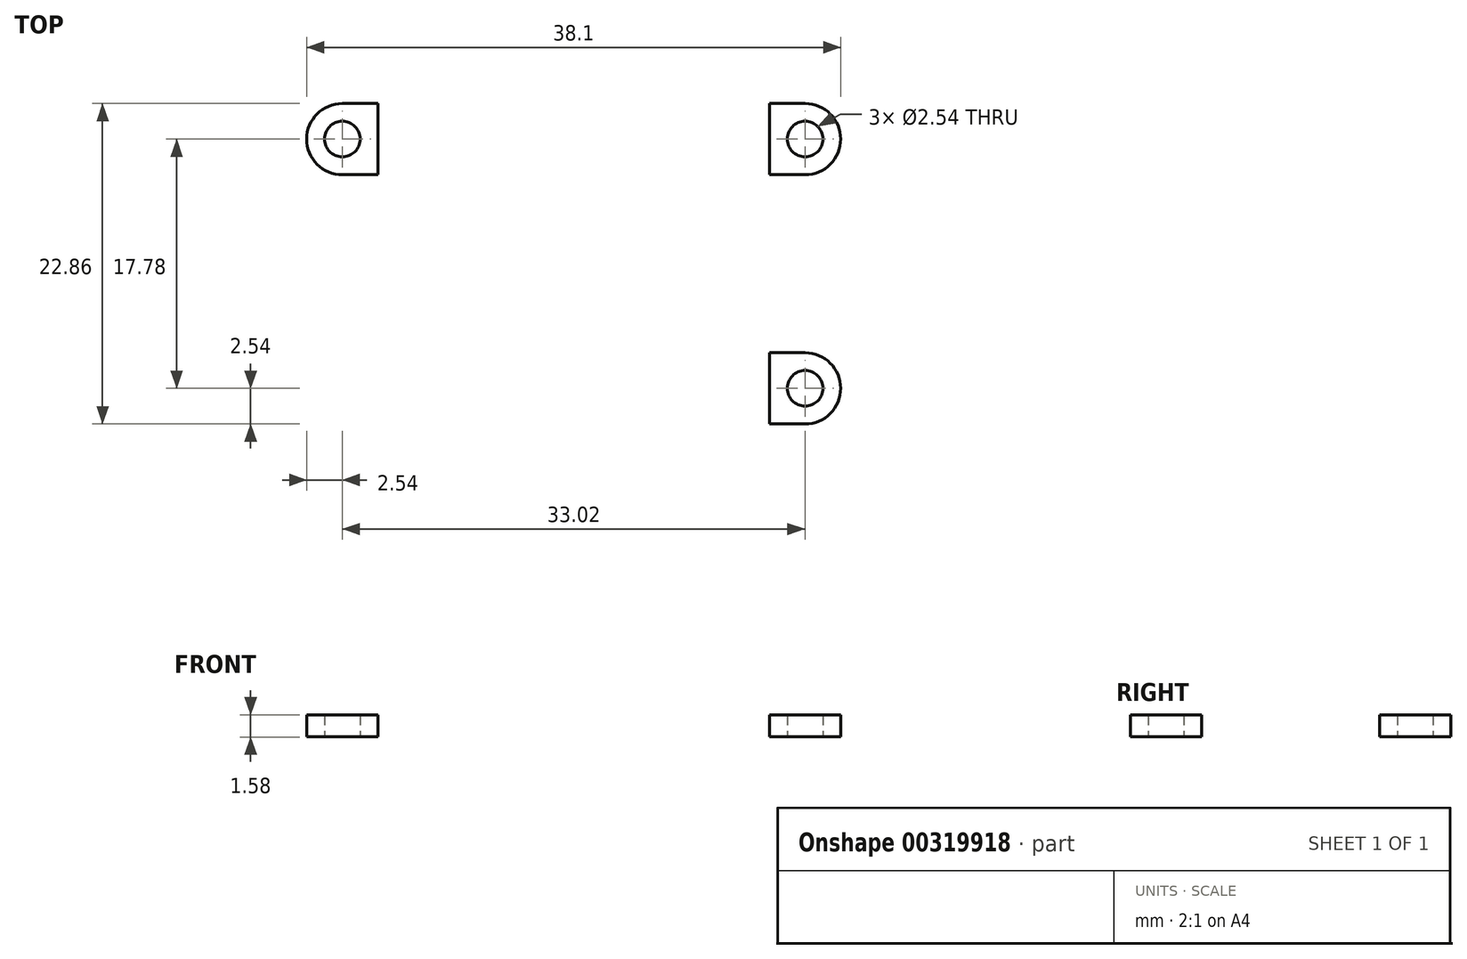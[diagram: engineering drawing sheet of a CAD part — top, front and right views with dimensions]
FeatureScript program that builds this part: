
annotation { "Feature Type Name" : "Feature", "Feature Type Description" : "" }
export const myFeature = defineFeature(function(context is Context, id is Id, definition is map)
    precondition{}
    {
        {
            var Q0;
            Q0=qCreatedBy(makeId("Top.planeOp"),FACE);
            var sketch = newSketch(context, id + "F0", { "sketchPlane" : qUnion([Q0])});
            skLineSegment(sketch, "E0.bottom", {"start": v(16.51, 11.43) * mm, "end": v(-16.51, 11.43) * mm});
            skLineSegment(sketch, "E0.top", {"start": v(16.51, -11.43) * mm, "end": v(-13.97, -11.43) * mm});
            skLineSegment(sketch, "E0.right", {"start": v(-19.05, 8.89) * mm, "end": v(-19.05, 8.89) * mm});
            skPoint(sketch, "E0.middle", {"position": v(0, 0) * mm});
            skLineSegment(sketch, "E1", {"start": v(-13.97, 11.43) * mm, "end": v(-13.97, -11.43) * mm});
            skLineSegment(sketch, "E2", {"start": v(-16.5, 6.35) * mm, "end": v(-13.97, 6.35) * mm});
            skCircle(sketch, "E3", {"center": v(-16.5, 8.89) * mm, "radius": 1.27 * mm});
            skPoint(sketch, "E3.centerSnap0", {"position": v(-16.5, 6.35) * mm});
            skPoint(sketch, "E3.centerSnap1", {"position": v(-19.05, 8.89) * mm});
            skPoint(sketch, "E4.visualSharp", {"position": v(-19.05, 11.43) * mm});
            skArc(sketch, "E4.filletArc", {"start": v(-16.51, 11.43) * mm, "mid": v(-18.3, 10.69) * mm, "end": v(-19.05, 8.89) * mm});
            skPoint(sketch, "E5.visualSharp", {"position": v(-19.05, 6.35) * mm});
            skArc(sketch, "E5.filletArc", {"start": v(-19.05, 8.89) * mm, "mid": v(-18.3, 7.1) * mm, "end": v(-16.5, 6.35) * mm});
            skLineSegment(sketch, "E6", {"start": v(-16.51, 11.43) * mm, "end": v(-13.97, 11.43) * mm});
            skPoint(sketch, "E7.MirrorP", {"position": v(-19.05, -8.89) * mm});
            skPoint(sketch, "E8.MirrorP", {"position": v(-19.05, -6.35) * mm});
            skCircle(sketch, "E9.MirrorC", {"center": v(-16.5, -8.89) * mm, "radius": 1.27 * mm});
            skArc(sketch, "E10.MirrorCS", {"start": v(-16.51, -11.43) * mm, "mid": v(-18.3, -10.69) * mm, "end": v(-19.05, -8.89) * mm});
            skPoint(sketch, "E11.MirrorP", {"position": v(-19.05, -11.43) * mm});
            skArc(sketch, "E12.MirrorCS", {"start": v(-19.05, -8.89) * mm, "mid": v(-18.3, -7.1) * mm, "end": v(-16.5, -6.35) * mm});
            skPoint(sketch, "E13.MirrorP", {"position": v(-16.5, -6.35) * mm});
            skLineSegment(sketch, "E14.MirrorCS", {"start": v(-16.5, -6.35) * mm, "end": v(-13.97, -6.35) * mm});
            skLineSegment(sketch, "E15.MirrorCS", {"start": v(-16.51, -11.43) * mm, "end": v(-13.97, -11.43) * mm});
            skLineSegment(sketch, "E16.MirrorCS", {"start": v(-13.97, -11.43) * mm, "end": v(-13.97, 11.43) * mm});
            skLineSegment(sketch, "E17.MirrorCS", {"start": v(-19.05, -8.89) * mm, "end": v(-19.05, -8.89) * mm});
            skPoint(sketch, "E18.MirrorP", {"position": v(19.05, 8.89) * mm});
            skPoint(sketch, "E19.MirrorP", {"position": v(19.05, -8.89) * mm});
            skPoint(sketch, "E20.MirrorP", {"position": v(16.5, -6.35) * mm});
            skPoint(sketch, "E21.MirrorP", {"position": v(16.5, 6.35) * mm});
            skCircle(sketch, "E22.MirrorC", {"center": v(16.5, 8.89) * mm, "radius": 1.27 * mm});
            skLineSegment(sketch, "E23.MirrorCS", {"start": v(16.5, -6.35) * mm, "end": v(13.97, -6.35) * mm});
            skLineSegment(sketch, "E24.MirrorCS", {"start": v(16.51, -11.43) * mm, "end": v(13.97, -11.43) * mm});
            skArc(sketch, "E25.MirrorCS", {"start": v(19.05, 8.89) * mm, "mid": v(18.3, 7.1) * mm, "end": v(16.5, 6.35) * mm});
            skLineSegment(sketch, "E26.MirrorCS", {"start": v(13.97, -11.43) * mm, "end": v(13.97, 11.43) * mm});
            skArc(sketch, "E27.MirrorCS", {"start": v(19.05, -8.89) * mm, "mid": v(18.3, -7.1) * mm, "end": v(16.5, -6.35) * mm});
            skArc(sketch, "E28.MirrorCS", {"start": v(16.51, -11.43) * mm, "mid": v(18.3, -10.69) * mm, "end": v(19.05, -8.89) * mm});
            skLineSegment(sketch, "E29.MirrorCS", {"start": v(16.51, 11.43) * mm, "end": v(13.97, 11.43) * mm});
            skLineSegment(sketch, "E30.MirrorCS", {"start": v(16.5, 6.35) * mm, "end": v(13.97, 6.35) * mm});
            skArc(sketch, "E31.MirrorCS", {"start": v(16.51, 11.43) * mm, "mid": v(18.3, 10.69) * mm, "end": v(19.05, 8.89) * mm});
            skPoint(sketch, "E32.MirrorP", {"position": v(19.05, -11.43) * mm});
            skCircle(sketch, "E33.MirrorC", {"center": v(16.5, -8.89) * mm, "radius": 1.27 * mm});
            skPoint(sketch, "E34.MirrorP", {"position": v(19.05, 11.43) * mm});
            skPoint(sketch, "E35.MirrorP", {"position": v(19.05, 6.35) * mm});
            skPoint(sketch, "E36.MirrorP", {"position": v(19.05, -6.35) * mm});
            skLineSegment(sketch, "E37.MirrorCS", {"start": v(13.97, 11.43) * mm, "end": v(13.97, -11.43) * mm});
            skSolve(sketch);
        }
        {
            var Q0;
            {var subQ5=sQuery(id+"F0.wireOp",EDGE,"E0.bottom");Q0=makeQuery(id+"F0.imprint","IMPRINT",FACE,{"disambiguationData":[TD([[makeQuery(id+"F0.imprint","IMPRINT",EDGE,{"derivedFrom":subQ5}),1.0]])]});}
            var Q1;
            Q1=makeQuery(id+"F0.imprint","IMPRINT",FACE,{"disambiguationData":[TD([[makeQuery(id+"F0.imprint","IMPRINT",EDGE,{"derivedFrom":sQuery(id+"F0.wireOp",EDGE,"E5.filletArc")}),1.0]])]});
            var Q2;
            Q2=makeQuery(id+"F0.imprint","IMPRINT",FACE,{"disambiguationData":[TD([[makeQuery(id+"F0.imprint","IMPRINT",EDGE,{"derivedFrom":sQuery(id+"F0.wireOp",EDGE,"E12.MirrorCS")}),-1.0]])]});
            var Q3;
            Q3=makeQuery(id+"F0.imprint","IMPRINT",FACE,{"disambiguationData":[TD([[makeQuery(id+"F0.imprint","IMPRINT",EDGE,{"derivedFrom":sQuery(id+"F0.wireOp",EDGE,"E33.MirrorC")}),-1.0]])]});
            var Q4;
            Q4=makeQuery(id+"F0.imprint","IMPRINT",FACE,{"disambiguationData":[TD([[makeQuery(id+"F0.imprint","IMPRINT",EDGE,{"derivedFrom":sQuery(id+"F0.wireOp",EDGE,"E25.MirrorCS")}),-1.0]])]});
            extrude(context, id + "F1", {"entities" : qUnion([Q0, Q1, Q2, Q3, Q4]), "depth" : 1.57 * mm, "symmetric" : true});
        }
    });
